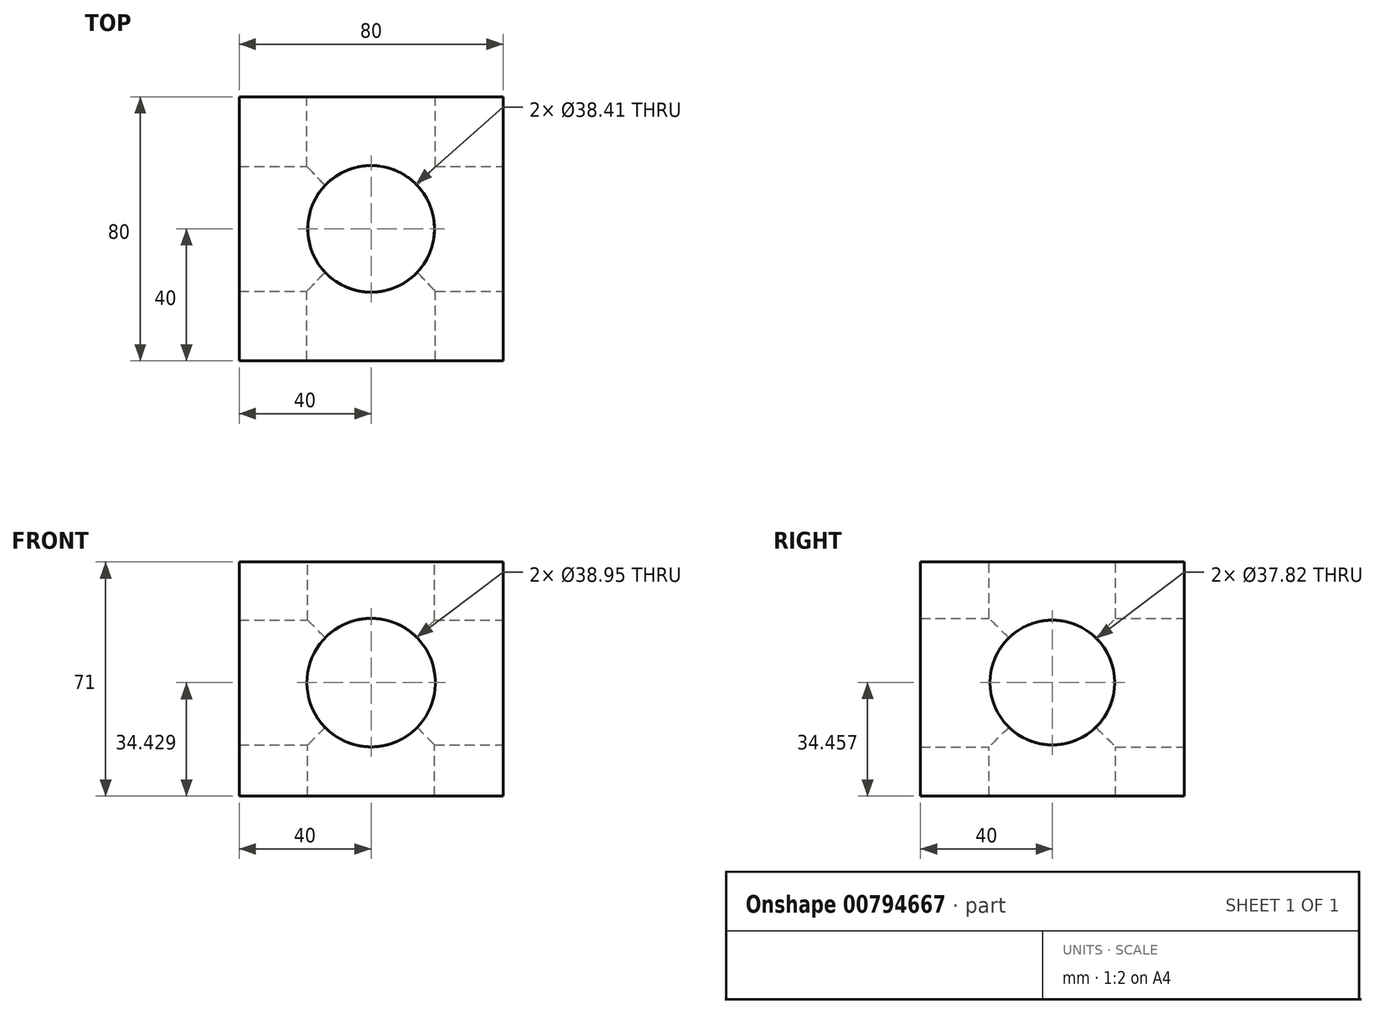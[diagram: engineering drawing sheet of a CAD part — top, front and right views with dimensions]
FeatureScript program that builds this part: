
annotation { "Feature Type Name" : "Feature", "Feature Type Description" : "" }
export const myFeature = defineFeature(function(context is Context, id is Id, definition is map)
    precondition{}
    {
        {
            var Q0;
            Q0=qCreatedBy(makeId("Top.planeOp"),FACE);
            var sketch = newSketch(context, id + "F0", { "sketchPlane" : qUnion([Q0])});
            skLineSegment(sketch, "E0.bottom", {"start": v(40, 40) * mm, "end": v(-40, 40) * mm});
            skLineSegment(sketch, "E0.top", {"start": v(40, -40) * mm, "end": v(-40, -40) * mm});
            skLineSegment(sketch, "E0.left", {"start": v(40, 40) * mm, "end": v(40, -40) * mm});
            skLineSegment(sketch, "E0.right", {"start": v(-40, 40) * mm, "end": v(-40, -40) * mm});
            skPoint(sketch, "E0.middle", {"position": v(0, 0) * mm});
            skSolve(sketch);
        }
        {
            var Q0;
            Q0 = qSketchRegion(id + "F0", true);
            extrude(context, id + "F1", {"entities" : qUnion([Q0]), "depth" : 71 * mm, "offsetDistance" : 25 * mm});
        }
        {
            var Q0;
            Q0=makeQuery(id+"F1.opExtrude","SWEPT_FACE",FACE,{"disambiguationData":[OSD([sQuery(id+"F0.wireOp",EDGE,"E0.left")])]});
            var sketch = newSketch(context, id + "F2", { "sketchPlane" : qUnion([Q0])});
            skCircle(sketch, "E1", {"center": v(0, 34.46) * mm, "radius": 18.9 * mm});
            skSolve(sketch);
        }
        {
            var Q0;
            Q0 = qSketchRegion(id + "F2", true);
            extrude(context, id + "F3", {"entities" : qUnion([Q0]), "operationType" : NewBodyOperationType.REMOVE, "oppositeDirection" : true, "depth" : 75 * mm, "offsetDistance" : 25 * mm});
        }
        {
            var Q0;
            Q0 = qSketchRegion(id + "F2", true);
            extrude(context, id + "F4", {"entities" : qUnion([Q0]), "operationType" : NewBodyOperationType.REMOVE, "oppositeDirection" : true, "depth" : 135 * mm, "offsetDistance" : 25 * mm});
        }
        {
            var Q0;
            Q0=makeQuery(id+"F1.opExtrude","SWEPT_FACE",FACE,{"disambiguationData":[OSD([sQuery(id+"F0.wireOp",EDGE,"E0.bottom")])]});
            var sketch = newSketch(context, id + "F5", { "sketchPlane" : qUnion([Q0])});
            skCircle(sketch, "E2", {"center": v(0, 34.43) * mm, "radius": 19.48 * mm});
            skSolve(sketch);
        }
        {
            var Q0;
            Q0 = qSketchRegion(id + "F5", true);
            extrude(context, id + "F6", {"entities" : qUnion([Q0]), "operationType" : NewBodyOperationType.REMOVE, "oppositeDirection" : true, "depth" : 94 * mm, "offsetDistance" : 25 * mm});
        }
        {
            var Q0;
            Q0=makeQuery(id+"F1.opExtrude","CAP_FACE",FACE,{"disambiguationData":[OSD([sQuery(id+"F0.wireOp",EDGE,"E0.bottom"),sQuery(id+"F0.wireOp",EDGE,"E0.top"),sQuery(id+"F0.wireOp",EDGE,"E0.left"),sQuery(id+"F0.wireOp",EDGE,"E0.right")])],"isStart":false});
            var sketch = newSketch(context, id + "F7", { "sketchPlane" : qUnion([Q0])});
            skCircle(sketch, "E3", {"center": v(0, 0) * mm, "radius": 19.2 * mm});
            skSolve(sketch);
        }
        {
            var Q0;
            Q0 = qSketchRegion(id + "F7", true);
            extrude(context, id + "F8", {"entities" : qUnion([Q0]), "operationType" : NewBodyOperationType.REMOVE, "oppositeDirection" : true, "depth" : 78 * mm, "offsetDistance" : 25 * mm});
        }
    });
